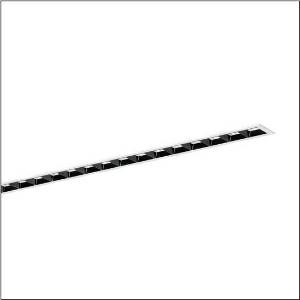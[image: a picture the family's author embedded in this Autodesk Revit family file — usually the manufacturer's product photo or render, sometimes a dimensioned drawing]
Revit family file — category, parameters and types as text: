
# Revit family: silica_21_51mx11da44wb
name_source: partatom
category: Lighting Fixtures
units: mm (PartAtom-declared; Revit-internal decimal feet)

## family parameters
Cut with Voids When Loaded = No
Host = Face
Light Source = No
Part Type = Normal
Room Calculation Point = No
Round Connector Dimension = Use Diameter
Shared = No

## types (1)
- --- (1 x LED, 4320 lm, 25.6 W, 4000K)
    Apparent Load = 26 VA
    CIE Flux Codes = 87 99 100 100 100
    Color Rendering = 80
    Color Temperature = 4000K
    Default Elevation = 1800 mm
    Description = Silica 21, office luminaire, primary light control with darklight reflector, of PMMA, black, CAT 2 (L<= 3000cd/m²), light emission: direct distribution, primary light characteristic: symmetric, installation type: recessed, LED, rated luminous flux: 4.320lm, luminous efficacy: 169lm/W, light colour: 840, colour temperature: 4000K, control gear: DALI 2, with terminal, 3+2-pole, max. 2.5mm², mains connection: 220..240V, AC, 50/60Hz, rated input power: 25.6W, luminaire housing, of aluminium, traffic white (RAL 9016), length: 1.228mm, width: 79mm, height: 53mm, protection rating (complete): IP20, insulation class (complete): insulation class I (protective earthing), certification: CE, ENEC, VDE, permissible operating ambient temperature: 0..+35°C, standard: EN 50419, packaging unit: 1 piece
    Height = 0 mm  [stored 0 ft]
    Lamp = 1 x LED
    Lamp Light Flux = 4320 lm
    Lamp Power = 25.6 W
    Lamp count = 1
    Length = 1227 mm
    Luminous efficacy = 169 lm/W
    Manufacturer = Siteco
    ModVariant = No
    Model = 51MX11DA44WB
    Mounting Place = Ceiling
    Mounting Type = Recessed
    Number of Poles = 1
    OnlyDefault = Yes
    Power Factor = 1
    Product Name = Silica 21
    Product group = office luminaire | ceiling recessed
    ProductGroupID = 400
    Protection Class = Protection class I
    Protection Degree = IP 20
    RLX_Detail_Level = 1
    RLX_Emergency_Light_Flux = 0 lm
    RLX_Emergency_Type = 0
    RLX_Emergency_Type_DB = No
    RlxData = <blob elided: 38961 chars, md5=f1522297>
    Socket = socket
    Standby Power = 0 W
    System Light Flux = 4320 lm
    System Power = 26 W
    Type Comments = factory setting: luminous flux: 100 % | dim-lin: 254 | 367 mA
    Type Image = l_1335880.jpg
    URL = http://relux.com
    VarID = @adj_028371
    Voltage = 0 V
    Weight = 0.00 kg
    Width = 79 mm

note: [stored X ft] marks values corroborated as IEEE doubles in the binary element streams (Revit-internal decimal feet)

## geometry (parser evidence)
native form markers: Blend x4, Sweep x12
no freeform markers — native parametric forms only
